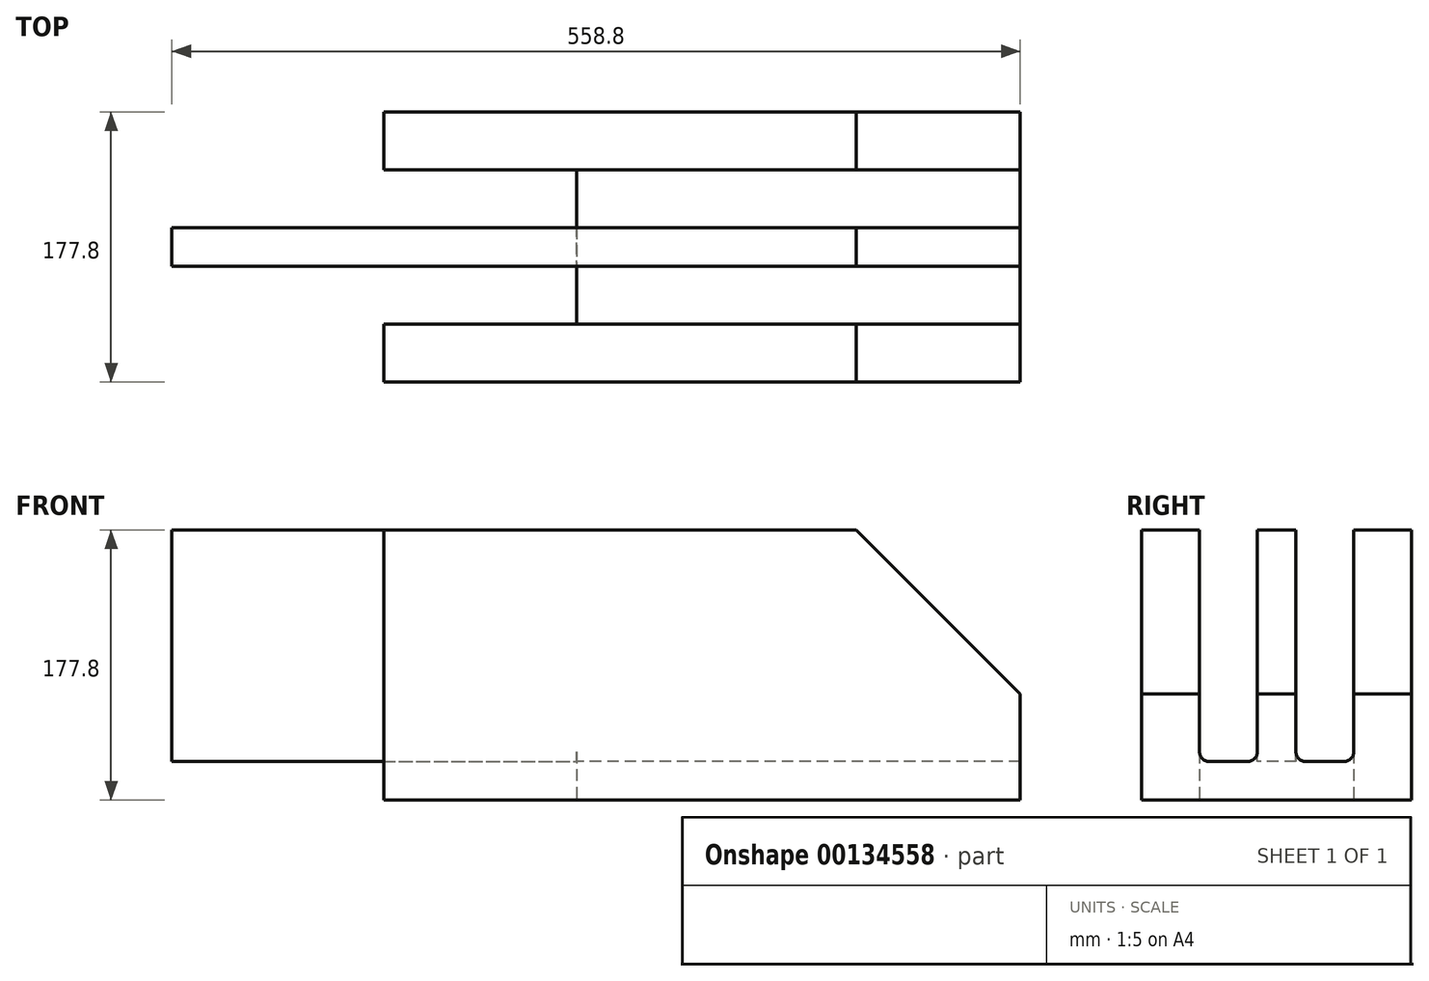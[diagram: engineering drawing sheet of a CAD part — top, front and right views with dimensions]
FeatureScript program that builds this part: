
annotation { "Feature Type Name" : "Feature", "Feature Type Description" : "" }
export const myFeature = defineFeature(function(context is Context, id is Id, definition is map)
    precondition{}
    {
        {
            var Q0;
            Q0=qCreatedBy(makeId("Top.planeOp"),FACE);
            var sketch = newSketch(context, id + "F0", { "sketchPlane" : qUnion([Q0])});
            skLineSegment(sketch, "E0", {"start": v(-28.5, 24.88) * mm, "end": v(390.6, 24.88) * mm});
            skLineSegment(sketch, "E1", {"start": v(390.6, 24.88) * mm, "end": v(390.6, -152.92) * mm});
            skLineSegment(sketch, "E2", {"start": v(390.6, -152.92) * mm, "end": v(-28.5, -152.92) * mm});
            skLineSegment(sketch, "E3", {"start": v(-28.5, -152.92) * mm, "end": v(-28.5, -114.82) * mm});
            skLineSegment(sketch, "E4", {"start": v(-28.5, -114.82) * mm, "end": v(98.5, -114.82) * mm});
            skLineSegment(sketch, "E5", {"start": v(98.5, -114.82) * mm, "end": v(98.5, -13.22) * mm});
            skLineSegment(sketch, "E6", {"start": v(98.5, -13.22) * mm, "end": v(-28.5, -13.22) * mm});
            skLineSegment(sketch, "E7", {"start": v(-28.5, -13.22) * mm, "end": v(-28.5, 24.88) * mm});
            skLineSegment(sketch, "E8", {"start": v(98.5, -64.02) * mm, "end": v(98.5, -57.67) * mm});
            skLineSegment(sketch, "E9", {"start": v(98.5, -57.67) * mm, "end": v(390.6, -57.67) * mm});
            skLineSegment(sketch, "E10", {"start": v(390.6, -57.67) * mm, "end": v(390.6, -70.37) * mm});
            skLineSegment(sketch, "E11", {"start": v(390.6, -70.37) * mm, "end": v(98.5, -70.37) * mm});
            skLineSegment(sketch, "E12", {"start": v(98.5, -70.37) * mm, "end": v(98.5, -57.67) * mm});
            skLineSegment(sketch, "E13", {"start": v(98.5, -114.82) * mm, "end": v(390.6, -114.82) * mm});
            skLineSegment(sketch, "E14", {"start": v(98.5, -13.22) * mm, "end": v(390.6, -13.22) * mm});
            skSolve(sketch);
        }
        {
            var Q0;
            Q0 = qSketchRegion(id + "F0", true);
            extrude(context, id + "F1", {"entities" : qUnion([Q0]), "depth" : 25.4 * mm});
        }
        {
            var Q0;
            Q0=makeQuery(id+"F1.opExtrude","CAP_FACE",FACE,{"disambiguationData":[OSD([sQuery(id+"F0.wireOp",EDGE,"E0"),sQuery(id+"F0.wireOp",EDGE,"E1"),sQuery(id+"F0.wireOp",EDGE,"E2"),sQuery(id+"F0.wireOp",EDGE,"E3"),sQuery(id+"F0.wireOp",EDGE,"E4"),sQuery(id+"F0.wireOp",EDGE,"E5"),sQuery(id+"F0.wireOp",EDGE,"E6"),sQuery(id+"F0.wireOp",EDGE,"E7"),sQuery(id+"F0.wireOp",EDGE,"E10"),sQuery(id+"F0.wireOp",EDGE,"E12")])],"isStart":false});
            cPlane(context, id + "F2", {"entities" : qUnion([Q0]), "cplaneType" : CPlaneType.OFFSET, "offset" : 0 * mm, "width" : 152.4 * mm, "height" : 152.4 * mm});
        }
        {
            var Q0;
            Q0=makeQuery(id+"F1.opExtrude","CAP_FACE",FACE,{"disambiguationData":[OSD([sQuery(id+"F0.wireOp",EDGE,"E0"),sQuery(id+"F0.wireOp",EDGE,"E1"),sQuery(id+"F0.wireOp",EDGE,"E2"),sQuery(id+"F0.wireOp",EDGE,"E3"),sQuery(id+"F0.wireOp",EDGE,"E4"),sQuery(id+"F0.wireOp",EDGE,"E5"),sQuery(id+"F0.wireOp",EDGE,"E6"),sQuery(id+"F0.wireOp",EDGE,"E7"),sQuery(id+"F0.wireOp",EDGE,"E10"),sQuery(id+"F0.wireOp",EDGE,"E12")])],"isStart":false});
            extrude(context, id + "F3", {"entities" : qUnion([Q0]), "operationType" : NewBodyOperationType.ADD, "depth" : 152.4 * mm});
        }
        {
            var Q0;
            Q0=makeQuery(id+"F3.opExtrude","CAP_FACE",FACE,{"disambiguationData":[OSD([sQuery(id+"F0.wireOp",EDGE,"E0"),sQuery(id+"F0.wireOp",EDGE,"E1"),sQuery(id+"F0.wireOp",EDGE,"E2"),sQuery(id+"F0.wireOp",EDGE,"E3"),sQuery(id+"F0.wireOp",EDGE,"E4"),sQuery(id+"F0.wireOp",EDGE,"E5"),sQuery(id+"F0.wireOp",EDGE,"E6"),sQuery(id+"F0.wireOp",EDGE,"E7"),sQuery(id+"F0.wireOp",EDGE,"E10"),sQuery(id+"F0.wireOp",EDGE,"E12")])],"isStart":false});
            var sketch = newSketch(context, id + "F4", { "sketchPlane" : qUnion([Q0])});
            skLineSegment(sketch, "E15", {"start": v(98.5, -13.22) * mm, "end": v(390.6, -13.22) * mm});
            skLineSegment(sketch, "E16", {"start": v(390.6, -13.22) * mm, "end": v(390.6, -51.32) * mm});
            skLineSegment(sketch, "E17", {"start": v(390.6, -51.32) * mm, "end": v(98.5, -51.32) * mm});
            skPoint(sketch, "E17.endSnap0", {"position": v(98.5, -64.02) * mm});
            skLineSegment(sketch, "E18", {"start": v(98.5, -51.32) * mm, "end": v(98.5, -13.22) * mm});
            skLineSegment(sketch, "E19", {"start": v(98.5, -114.82) * mm, "end": v(98.5, -76.72) * mm});
            skLineSegment(sketch, "E20", {"start": v(390.6, -76.72) * mm, "end": v(98.5, -76.72) * mm});
            skLineSegment(sketch, "E21", {"start": v(98.5, -114.82) * mm, "end": v(390.6, -114.82) * mm});
            skLineSegment(sketch, "E22", {"start": v(390.6, -114.82) * mm, "end": v(390.6, -76.72) * mm});
            skSolve(sketch);
        }
        {
            var Q0;
            Q0=makeQuery(id+"F4.imprint","IMPRINT",FACE,{"disambiguationData":[TD([[makeQuery(id+"F4.imprint","IMPRINT",EDGE,{"derivedFrom":sQuery(id+"F4.wireOp",EDGE,"E15")}),-1.0]])]});
            var Q1;
            Q1=makeQuery(id+"F4.imprint","IMPRINT",FACE,{"disambiguationData":[TD([[makeQuery(id+"F4.imprint","IMPRINT",EDGE,{"derivedFrom":sQuery(id+"F4.wireOp",EDGE,"E19")}),-1.0]])]});
            extrude(context, id + "F5", {"entities" : qUnion([Q0, Q1]), "operationType" : NewBodyOperationType.REMOVE, "oppositeDirection" : true, "depth" : 152.4 * mm});
        }
        {
            var Q0;
            {var subQ0=sQuery(id+"F0.wireOp",EDGE,"E10");var subQ1=sQuery(id+"F0.wireOp",EDGE,"E1");var subQ2=sQuery(id+"F0.wireOp",EDGE,"E2");Q0=makeQuery(id+"F5.boolean.opBoolean","SPLIT",EDGE,{"disambiguationData":[TD([makeQuery(id+"F1.opExtrude","SWEPT_FACE",FACE,{"disambiguationData":[OSD([subQ2])]})])],"derivedFrom":makeQuery(id+"F3.opExtrude","CAP_EDGE",EDGE,{"disambiguationData":[OSD([subQ1,subQ0])],"isStart":false})});}
            var Q1;
            {var subQ0=sQuery(id+"F0.wireOp",EDGE,"E10");var subQ1=sQuery(id+"F0.wireOp",EDGE,"E1");Q1=makeQuery(id+"F5.boolean.opBoolean","SPLIT",EDGE,{"disambiguationData":[TD([makeQuery(id+"F5.opExtrude","SWEPT_FACE",FACE,{"disambiguationData":[OSD([sQuery(id+"F4.wireOp",EDGE,"E17")])]})])],"derivedFrom":makeQuery(id+"F3.opExtrude","CAP_EDGE",EDGE,{"disambiguationData":[OSD([subQ1,subQ0])],"isStart":false})});}
            var Q2;
            {var subQ1=sQuery(id+"F0.wireOp",EDGE,"E10");var subQ2=sQuery(id+"F0.wireOp",EDGE,"E1");var subQ3=sQuery(id+"F0.wireOp",EDGE,"E0");Q2=makeQuery(id+"F5.boolean.opBoolean","SPLIT",EDGE,{"disambiguationData":[TD([makeQuery(id+"F1.opExtrude","SWEPT_FACE",FACE,{"disambiguationData":[OSD([subQ3])]})])],"derivedFrom":makeQuery(id+"F3.opExtrude","CAP_EDGE",EDGE,{"disambiguationData":[OSD([subQ2,subQ1])],"isStart":false})});}
            chamfer(context, id + "F6", {"entities" : qUnion([Q0, Q1, Q2]), "width" : 107.95 * mm, "tangentPropagation" : true});
        }
        {
            var Q0;
            {var subQ0=sQuery(id+"F0.wireOp",EDGE,"E12");var subQ1=sQuery(id+"F0.wireOp",EDGE,"E5");Q0=makeQuery(id+"F3.boolean.opBoolean","MERGE",FACE,{"derivedFrom":[makeQuery(id+"F1.opExtrude","SWEPT_FACE",FACE,{"disambiguationData":[OSD([subQ1,subQ0])]}),makeQuery(id+"F3.opExtrude","SWEPT_FACE",FACE,{"disambiguationData":[OSD([subQ1,subQ0])]})]});}
            var sketch = newSketch(context, id + "F7", { "sketchPlane" : qUnion([Q0])});
            skLineSegment(sketch, "E23", {"start": v(51.32, 25.4) * mm, "end": v(76.72, 25.4) * mm});
            skLineSegment(sketch, "E24", {"start": v(76.72, 25.4) * mm, "end": v(76.72, 177.8) * mm});
            skLineSegment(sketch, "E25", {"start": v(76.72, 177.8) * mm, "end": v(51.32, 177.8) * mm});
            skLineSegment(sketch, "E26", {"start": v(51.32, 177.8) * mm, "end": v(51.32, 25.4) * mm});
            skSolve(sketch);
        }
        {
            var Q0;
            Q0 = qSketchRegion(id + "F7", true);
            extrude(context, id + "F8", {"entities" : qUnion([Q0]), "operationType" : NewBodyOperationType.ADD, "depth" : 266.7 * mm});
        }
        {
            var Q0;
            Q0=makeQuery(id+"F5.boolean.opBoolean","COPY",EDGE,{"derivedFrom":makeQuery(id+"F5.opExtrude","CAP_EDGE",EDGE,{"disambiguationData":[OSD([sQuery(id+"F4.wireOp",EDGE,"E21")])],"isStart":false})});
            fillet(context, id + "F9", {"entities" : qUnion([Q0]), "radius" : 6.35 * mm, "tangentPropagation" : true, "allowEdgeOverflow" : false});
        }
        {
            var Q0;
            Q0=makeQuery(id+"F5.boolean.opBoolean","COPY",EDGE,{"derivedFrom":makeQuery(id+"F5.opExtrude","CAP_EDGE",EDGE,{"disambiguationData":[OSD([sQuery(id+"F4.wireOp",EDGE,"E17")])],"isStart":false})});
            var Q1;
            Q1=makeQuery(id+"F5.boolean.opBoolean","COPY",EDGE,{"derivedFrom":makeQuery(id+"F5.opExtrude","CAP_EDGE",EDGE,{"disambiguationData":[OSD([sQuery(id+"F4.wireOp",EDGE,"E20")])],"isStart":false})});
            var Q2;
            Q2=makeQuery(id+"F5.boolean.opBoolean","COPY",EDGE,{"derivedFrom":makeQuery(id+"F5.opExtrude","CAP_EDGE",EDGE,{"disambiguationData":[OSD([sQuery(id+"F4.wireOp",EDGE,"E15")])],"isStart":false})});
            fillet(context, id + "F10", {"entities" : qUnion([Q0, Q1, Q2]), "radius" : 6.35 * mm, "tangentPropagation" : true, "allowEdgeOverflow" : false});
        }
    });
